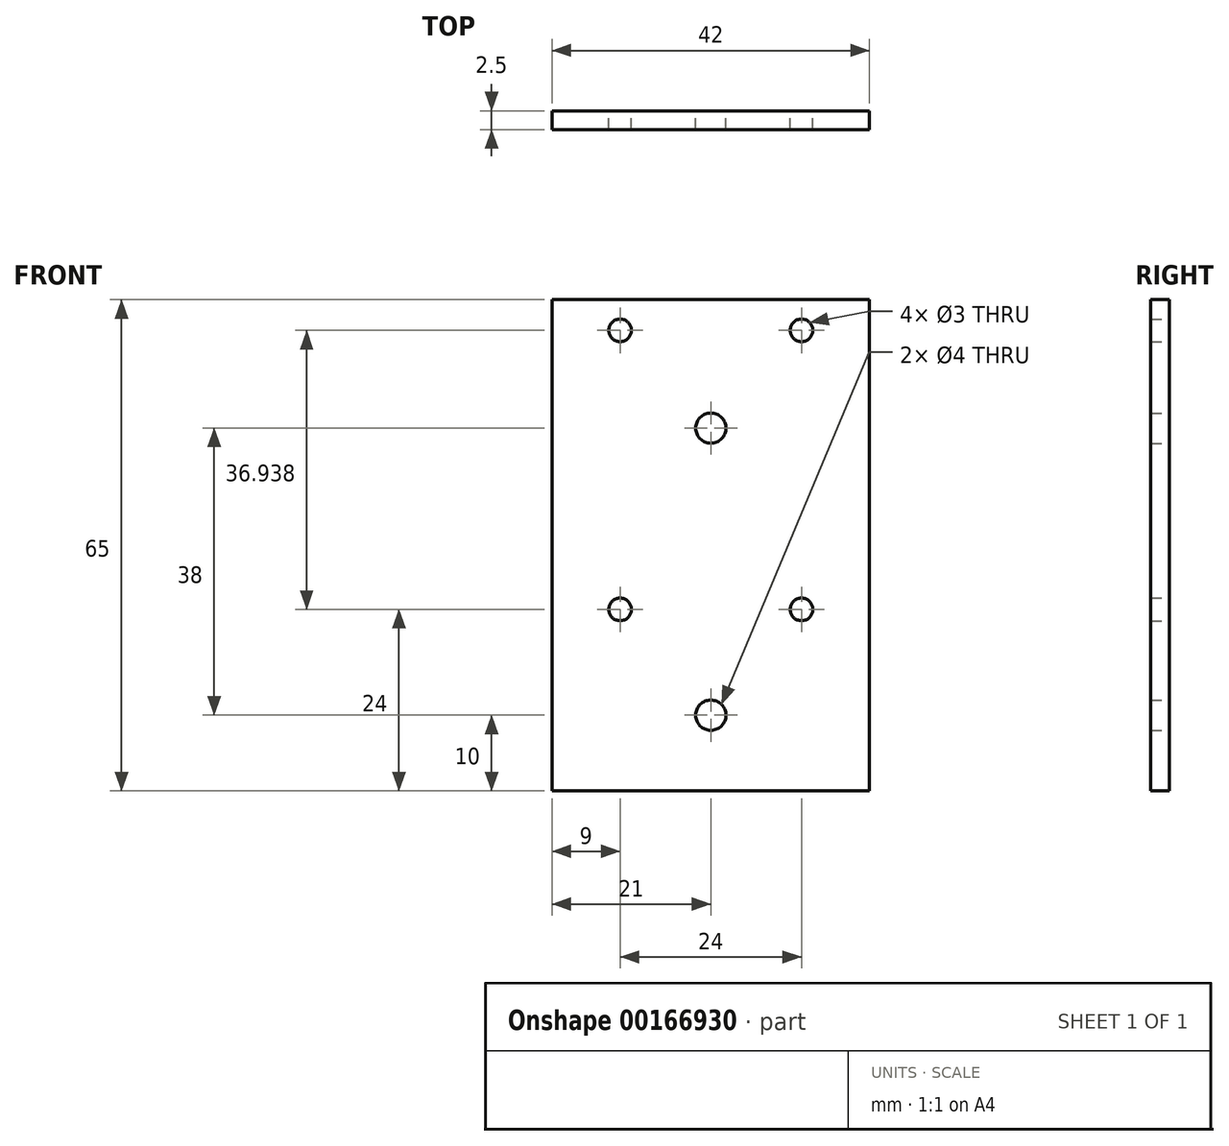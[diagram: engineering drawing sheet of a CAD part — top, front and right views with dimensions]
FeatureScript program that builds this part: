
annotation { "Feature Type Name" : "Feature", "Feature Type Description" : "" }
export const myFeature = defineFeature(function(context is Context, id is Id, definition is map)
    precondition{}
    {
        {
            var Q0;
            Q0=qCreatedBy(makeId("Front.planeOp"),FACE);
            var sketch = newSketch(context, id + "F0", { "sketchPlane" : qUnion([Q0])});
            skCircle(sketch, "E0", {"center": v(0, -22.5) * mm, "radius": 2 * mm});
            skCircle(sketch, "E1", {"center": v(0, 15.5) * mm, "radius": 2 * mm});
            skLineSegment(sketch, "E2", {"start": v(-21, -32.5) * mm, "end": v(-21, 32.5) * mm});
            skLineSegment(sketch, "E3", {"start": v(-21, 32.5) * mm, "end": v(21, 32.5) * mm});
            skLineSegment(sketch, "E4", {"start": v(21, 32.5) * mm, "end": v(21, -32.5) * mm});
            skLineSegment(sketch, "E5", {"start": v(21, -32.5) * mm, "end": v(-21, -32.5) * mm});
            skCircle(sketch, "E6", {"center": v(-12, 28.44) * mm, "radius": 1.5 * mm});
            skCircle(sketch, "E7", {"center": v(12, 28.44) * mm, "radius": 1.5 * mm});
            skCircle(sketch, "E8", {"center": v(-12, -8.5) * mm, "radius": 1.5 * mm});
            skCircle(sketch, "E9", {"center": v(12, -8.5) * mm, "radius": 1.5 * mm});
            skSolve(sketch);
        }
        {
            var Q0;
            Q0=qSketchRegion(id+"F0",true);
            extrude(context, id + "F1", {"entities" : qUnion([Q0]), "endBound" : BoundingType.SYMMETRIC, "depth" : 2.5 * mm});
        }
    });
